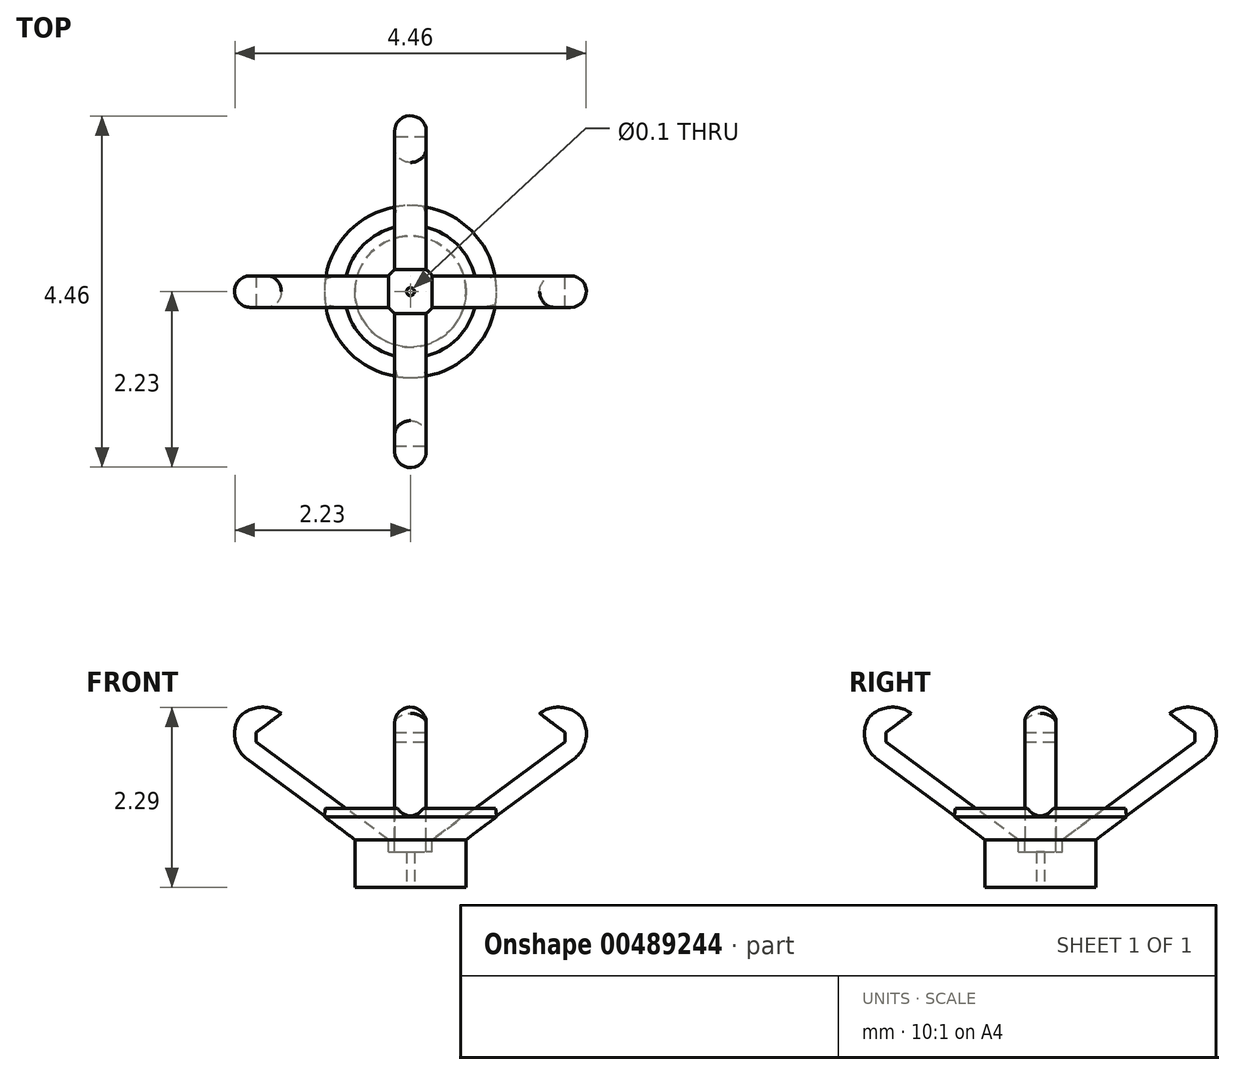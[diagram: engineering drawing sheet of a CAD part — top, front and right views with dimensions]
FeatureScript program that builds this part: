
annotation { "Feature Type Name" : "Feature", "Feature Type Description" : "" }
export const myFeature = defineFeature(function(context is Context, id is Id, definition is map)
    precondition{}
    {
        {
            var Q0;
            Q0=qCreatedBy(makeId("Right.planeOp"),FACE);
            var sketch = newSketch(context, id + "F0", { "sketchPlane" : qUnion([Q0])});
            skLineSegment(sketch, "E0", {"start": v(0, 0) * mm, "end": v(1.96, 1.45) * mm});
            skLineSegment(sketch, "E1", {"start": v(1.64, 1.81) * mm, "end": v(1.64, 1.81) * mm});
            skLineSegment(sketch, "E2", {"start": v(2.07, 1.23) * mm, "end": v(0.4, 0) * mm});
            skLineSegment(sketch, "E3", {"start": v(0.4, 0) * mm, "end": v(0, 0) * mm});
            skLineSegment(sketch, "E4", {"start": v(0.4, 0) * mm, "end": v(0.4, -0.4) * mm});
            skLineSegment(sketch, "E5", {"start": v(0.4, -0.4) * mm, "end": v(0, -0.4) * mm});
            skLineSegment(sketch, "E6", {"start": v(0, -0.4) * mm, "end": v(0, 0) * mm});
            skPoint(sketch, "E7.visualSharp", {"position": v(1.96, 2.05) * mm});
            skArc(sketch, "E7.filletArc", {"start": v(2.18, 1.76) * mm, "mid": v(1.92, 1.89) * mm, "end": v(1.64, 1.81) * mm});
            skLineSegment(sketch, "E8", {"start": v(1.96, 1.45) * mm, "end": v(1.96, 1.57) * mm});
            skLineSegment(sketch, "E9", {"start": v(1.96, 1.57) * mm, "end": v(1.64, 1.81) * mm});
            skLineSegment(sketch, "E10", {"start": v(1.96, 1.57) * mm, "end": v(1.43, 1.57) * mm, "construction": true});
            skPoint(sketch, "E11.visualSharp", {"position": v(2.42, 1.51) * mm});
            skArc(sketch, "E11.filletArc", {"start": v(2.07, 1.23) * mm, "mid": v(2.23, 1.48) * mm, "end": v(2.18, 1.76) * mm});
            skSolve(sketch);
        }
        {
            var Q0;
            Q0=qCreatedBy(makeId("Right.planeOp"),FACE);
            var sketch = newSketch(context, id + "F1", { "sketchPlane" : qUnion([Q0])});
            skLineSegment(sketch, "E12", {"start": v(0, 0) * mm, "end": v(0, 2) * mm, "construction": true});
            skSolve(sketch);
        }
        {
            var Q0;
            Q0=makeQuery(id+"F0.imprint","IMPRINT",FACE,{"disambiguationData":[TD([[makeQuery(id+"F0.imprint","IMPRINT",EDGE,{"derivedFrom":sQuery(id+"F0.wireOp",EDGE,"E3")}),1.0]])]});
            var Q1;
            Q1=sQuery(id+"F1.wireOp",EDGE,"E12");
            revolve(context, id + "F2", {"entities" : qUnion([Q0]), "axis" : qUnion([Q1]), "revolveType" : RevolveType.FULL});
        }
        {
            var Q0;
            Q0=makeQuery(id+"F0.imprint","IMPRINT",FACE,{"disambiguationData":[TD([[makeQuery(id+"F0.imprint","IMPRINT",EDGE,{"derivedFrom":sQuery(id+"F0.wireOp",EDGE,"E0")}),-1.0]])]});
            extrude(context, id + "F3", {"entities" : qUnion([Q0]), "operationType" : NewBodyOperationType.ADD, "endBound" : BoundingType.SYMMETRIC, "depth" : 0.4 * mm});
        }
        {
            var Q0;
            Q0=makeQuery(id+"F3.opExtrude","CAP_EDGE",EDGE,{"disambiguationData":[OSD([sQuery(id+"F0.wireOp",EDGE,"E7.filletArc")])],"isStart":false});
            var Q1;
            Q1=makeQuery(id+"F3.opExtrude","CAP_EDGE",EDGE,{"disambiguationData":[OSD([sQuery(id+"F0.wireOp",EDGE,"E7.filletArc")])],"isStart":true});
            var Q2;
            Q2=makeQuery(id+"F3.opExtrude","CAP_EDGE",EDGE,{"disambiguationData":[OSD([sQuery(id+"F0.wireOp",EDGE,"E2")])],"isStart":false});
            var Q3;
            Q3=makeQuery(id+"F3.opExtrude","CAP_EDGE",EDGE,{"disambiguationData":[OSD([sQuery(id+"F0.wireOp",EDGE,"E11.filletArc")])],"isStart":false});
            var Q4;
            Q4=makeQuery(id+"F3.opExtrude","CAP_EDGE",EDGE,{"disambiguationData":[OSD([sQuery(id+"F0.wireOp",EDGE,"E2")])],"isStart":true});
            var Q5;
            Q5=makeQuery(id+"F3.opExtrude","CAP_EDGE",EDGE,{"disambiguationData":[OSD([sQuery(id+"F0.wireOp",EDGE,"E11.filletArc")])],"isStart":true});
            var Q6;
            Q6=makeQuery(id+"F3.opExtrude","SWEPT_EDGE",EDGE,{"disambiguationData":[OSD([sQuery(id+"F0.wireOp",EDGE,"E7.filletArc"),sQuery(id+"F0.wireOp",EDGE,"E11.filletArc")])]});
            fillet(context, id + "F4", {"entities" : qUnion([Q0, Q1, Q2, Q3, Q4, Q5, Q6]), "radius" : 0.2 * mm, "tangentPropagation" : true, "allowEdgeOverflow" : false});
        }
        {
            var Q0;
            Q0=makeQuery(id+"F2.opRevolve","SWEPT_BODY",BODY,{"disambiguationData":[OSD([sQuery(id+"F0.wireOp",EDGE,"E3"),sQuery(id+"F0.wireOp",EDGE,"E4"),sQuery(id+"F0.wireOp",EDGE,"E5"),sQuery(id+"F0.wireOp",EDGE,"E6")])]});
            var Q1;
            Q1=sQuery(id+"F1.wireOp",EDGE,"E12");
            circularPattern(context, id + "F5", {"entities" : qUnion([Q0]), "axis" : qUnion([Q1]), "angle" : 360 * degree, "instanceCount" : 4, "equalSpace" : true});
        }
        {
            var Q0;
            Q0=makeQuery(id+"F5.opPattern","COPY",BODY,{"derivedFrom":makeQuery(id+"F2.opRevolve","SWEPT_BODY",BODY,{"disambiguationData":[OSD([sQuery(id+"F0.wireOp",EDGE,"E3"),sQuery(id+"F0.wireOp",EDGE,"E4"),sQuery(id+"F0.wireOp",EDGE,"E5"),sQuery(id+"F0.wireOp",EDGE,"E6")])]}),"instanceName":"3"});
            var Q1;
            Q1=makeQuery(id+"F5.opPattern","COPY",BODY,{"derivedFrom":makeQuery(id+"F2.opRevolve","SWEPT_BODY",BODY,{"disambiguationData":[OSD([sQuery(id+"F0.wireOp",EDGE,"E3"),sQuery(id+"F0.wireOp",EDGE,"E4"),sQuery(id+"F0.wireOp",EDGE,"E5"),sQuery(id+"F0.wireOp",EDGE,"E6")])]}),"instanceName":"2"});
            var Q2;
            Q2=makeQuery(id+"F2.opRevolve","SWEPT_BODY",BODY,{"disambiguationData":[OSD([sQuery(id+"F0.wireOp",EDGE,"E3"),sQuery(id+"F0.wireOp",EDGE,"E4"),sQuery(id+"F0.wireOp",EDGE,"E5"),sQuery(id+"F0.wireOp",EDGE,"E6")])]});
            var Q3;
            Q3=makeQuery(id+"F5.opPattern","COPY",BODY,{"derivedFrom":makeQuery(id+"F2.opRevolve","SWEPT_BODY",BODY,{"disambiguationData":[OSD([sQuery(id+"F0.wireOp",EDGE,"E3"),sQuery(id+"F0.wireOp",EDGE,"E4"),sQuery(id+"F0.wireOp",EDGE,"E5"),sQuery(id+"F0.wireOp",EDGE,"E6")])]}),"instanceName":"1"});
            booleanBodies(context, id + "F6", {"operationType" : BooleanOperationType.UNION, "tools" : qUnion([Q0, Q1, Q2, Q3])});
        }
        {
            var Q0;
            Q0=makeQuery(id+"F5.opPattern","COPY",FACE,{"derivedFrom":makeQuery(id+"F2.opRevolve","SWEPT_FACE",FACE,{"disambiguationData":[OSD([sQuery(id+"F0.wireOp",EDGE,"E5")])]}),"instanceName":"3"});
            var sketch = newSketch(context, id + "F7", { "sketchPlane" : qUnion([Q0])});
            skCircle(sketch, "E13", {"center": v(0, 0) * mm, "radius": 0.05 * mm});
            skSolve(sketch);
        }
        {
            var Q0;
            {var subQ0=makeQuery(id+"F4.opFillet","BLEND_FACE",FACE,{"disambiguationData":[OSD([sQuery(id+"F0.wireOp",EDGE,"E2")])]});var subQ1=makeQuery(id+"F5.opPattern","COPY",FACE,{"derivedFrom":makeQuery(id+"F2.opRevolve","SWEPT_FACE",FACE,{"disambiguationData":[OSD([sQuery(id+"F0.wireOp",EDGE,"E3")])]}),"instanceName":"3"});Q0=makeQuery(id+"F6.opBoolean","SPLIT",FACE,{"disambiguationData":[TD([subQ0,makeQuery(id+"F5.opPattern","COPY",FACE,{"derivedFrom":subQ0,"instanceName":"1"}),makeQuery(id+"F5.opPattern","COPY",FACE,{"derivedFrom":makeQuery(id+"F2.opRevolve","SWEPT_FACE",FACE,{"disambiguationData":[OSD([sQuery(id+"F0.wireOp",EDGE,"E4")])]}),"instanceName":"3"}),subQ1])],"derivedFrom":subQ1});}
            var sketch = newSketch(context, id + "F8", { "sketchPlane" : qUnion([Q0])});
            skCircle(sketch, "E14", {"center": v(-0.24, 0.25) * mm, "radius": 0.1 * mm});
            skSolve(sketch);
        }
        {
            var Q0;
            {var subQ0=sQuery(id+"F8.wireOp",EDGE,"E14");var subQ3=sQuery(id+"F0.wireOp",EDGE,"E3");var subQ4=makeQuery(id+"F2.opRevolve","SWEPT_FACE",FACE,{"disambiguationData":[OSD([subQ3])]});var subQ5=subQ4;var subQ6=makeQuery(id+"F5.opPattern","COPY",FACE,{"derivedFrom":subQ5,"instanceName":"3"});var subQ19=makeQuery(id+"F6.opBoolean","INTERSECT",EDGE,{"disambiguationData":[OD(1.0)],"derivedFrom":[subQ5,makeQuery(id+"F5.opPattern","COPY",FACE,{"derivedFrom":subQ5,"instanceName":"2"}),subQ6]});var subQ20=makeQuery(id+"F8.imprint","INTERSECT",VERTEX,{"derivedFrom":[subQ19,subQ0]});Q0=makeQuery(id+"F8.imprint","IMPRINT",FACE,{"disambiguationData":[TD([[makeQuery(id+"F8.imprint","IMPRINT",EDGE,{"disambiguationData":[TD([[subQ20,1.0]])],"derivedFrom":subQ0}),-1.0]])]});}
            cPlane(context, id + "F9", {"entities" : qUnion([Q0]), "cplaneType" : CPlaneType.OFFSET, "offset" : 1.2 * mm, "width" : 150 * mm, "height" : 150 * mm});
        }
        {
            var Q0;
            Q0=makeQuery(id+"F5.opPattern","COPY",FACE,{"derivedFrom":makeQuery(id+"F3.opExtrude","CAP_FACE",FACE,{"disambiguationData":[OSD([sQuery(id+"F0.wireOp",EDGE,"E0"),sQuery(id+"F0.wireOp",EDGE,"E2"),sQuery(id+"F0.wireOp",EDGE,"E3"),sQuery(id+"F0.wireOp",EDGE,"E7.filletArc"),sQuery(id+"F0.wireOp",EDGE,"E8"),sQuery(id+"F0.wireOp",EDGE,"E9"),sQuery(id+"F0.wireOp",EDGE,"E11.filletArc")])],"isStart":true}),"instanceName":"2"});
            var sketch = newSketch(context, id + "F10", { "sketchPlane" : qUnion([Q0])});
            skLineSegment(sketch, "E15", {"start": v(-0.82, 0.6) * mm, "end": v(-1.08, 0.6) * mm});
            skLineSegment(sketch, "E16", {"start": v(-1.08, 0.6) * mm, "end": v(-1.08, 0.5) * mm});
            skLineSegment(sketch, "E17", {"start": v(-0.68, 0.2) * mm, "end": v(-0.28, 0.2) * mm});
            skLineSegment(sketch, "E18", {"start": v(-0.28, 0.2) * mm, "end": v(-0.82, 0.6) * mm});
            skLineSegment(sketch, "E19", {"start": v(-0.68, 0.2) * mm, "end": v(-1.08, 0.5) * mm});
            skSolve(sketch);
        }
        {
            var Q0;
            Q0 = qSketchRegion(id + "F10", true);
            var Q1;
            Q1=sQuery(id+"F1.wireOp",EDGE,"E12");
            revolve(context, id + "F11", {"operationType" : NewBodyOperationType.ADD, "entities" : qUnion([Q0]), "axis" : qUnion([Q1]), "revolveType" : RevolveType.FULL});
        }
        {
            var Q0;
            Q0=makeQuery(id+"F11.opRevolve","SWEPT_FACE",FACE,{"disambiguationData":[OSD([sQuery(id+"F10.wireOp",EDGE,"E17")])]});
            var sketch = newSketch(context, id + "F12", { "sketchPlane" : qUnion([Q0])});
            skCircle(sketch, "E20", {"center": v(0, 0) * mm, "radius": 0.7 * mm});
            skSolve(sketch);
        }
        {
            var Q0;
            Q0 = qSketchRegion(id + "F12", true);
            var Q1;
            Q1=makeQuery(id+"F5.opPattern","COPY",FACE,{"derivedFrom":makeQuery(id+"F2.opRevolve","SWEPT_FACE",FACE,{"disambiguationData":[OSD([sQuery(id+"F0.wireOp",EDGE,"E5")])]}),"instanceName":"3"});
            extrude(context, id + "F13", {"entities" : qUnion([Q0]), "operationType" : NewBodyOperationType.ADD, "endBound" : BoundingType.UP_TO_SURFACE, "endBoundEntityFace" : qUnion([Q1]), "depth" : 25 * mm});
        }
        {
            var Q0;
            Q0 = qSketchRegion(id + "F7", true);
            extrude(context, id + "F14", {"entities" : qUnion([Q0]), "operationType" : NewBodyOperationType.REMOVE, "endBound" : BoundingType.THROUGH_ALL, "oppositeDirection" : true, "depth" : (0) * mm});
        }
        {
            var Q0;
            {var subQ0=makeQuery(id+"F3.opExtrude","SWEPT_FACE",FACE,{"disambiguationData":[OSD([sQuery(id+"F0.wireOp",EDGE,"E0")])]});Q0=makeQuery(id+"F13.boolean.opBoolean","SPLIT",FACE,{"disambiguationData":[TD([subQ0])],"derivedFrom":makeQuery(id+"F13.opExtrude","CAP_FACE",FACE,{"disambiguationData":[OSD([sQuery(id+"F12.wireOp",EDGE,"E20")])],"isStart":true})});}
            extrude(context, id + "F15", {"entities" : qUnion([Q0]), "operationType" : NewBodyOperationType.REMOVE, "oppositeDirection" : true, "depth" : 0.15 * mm});
        }
    });
